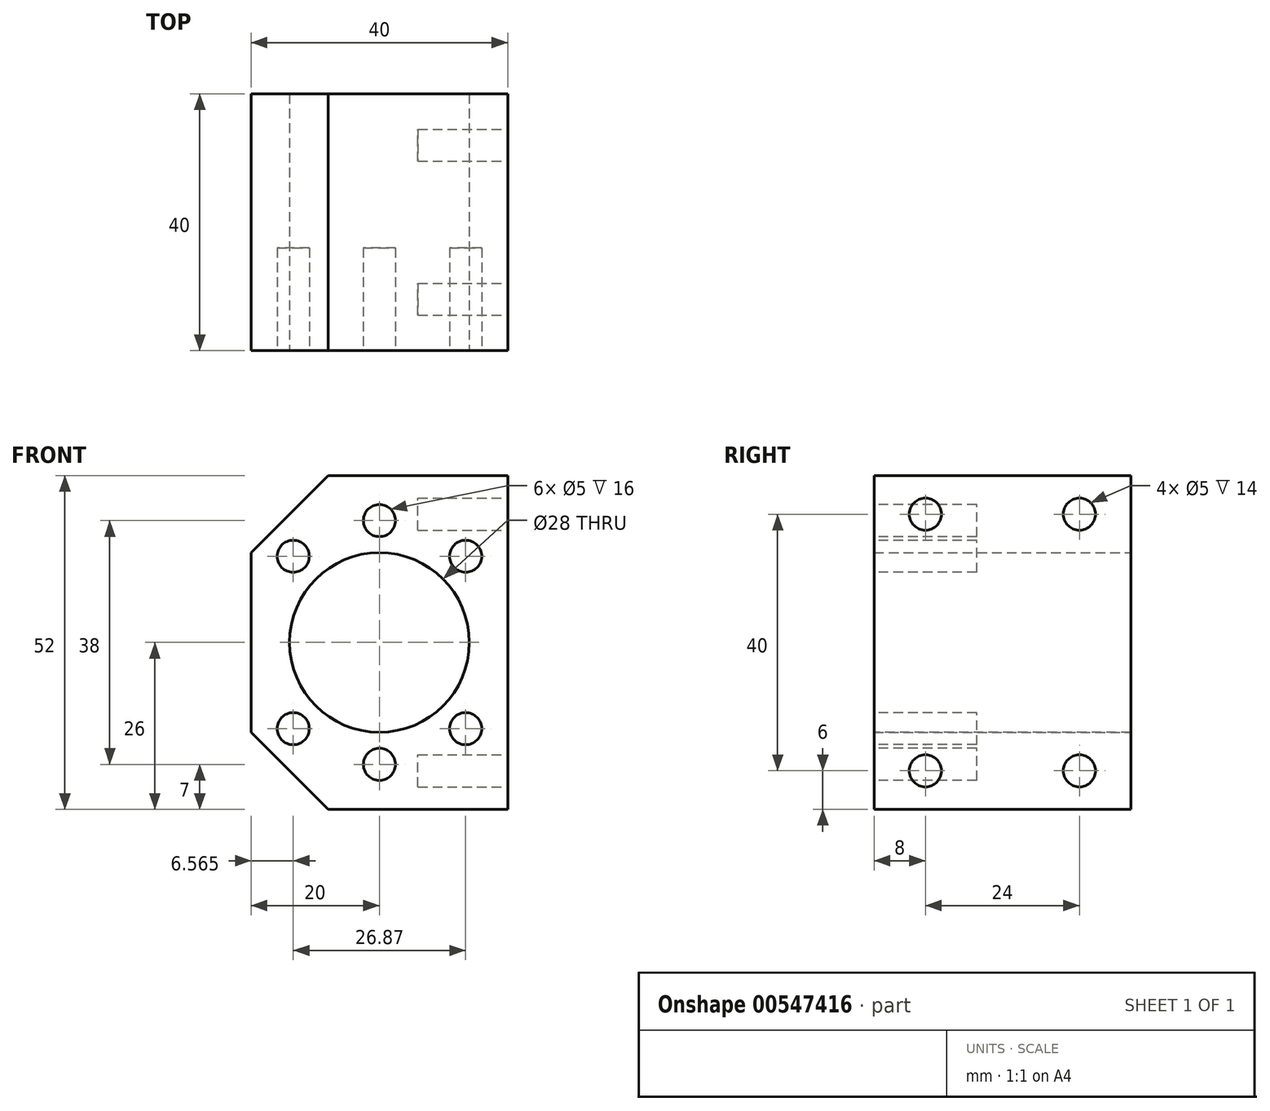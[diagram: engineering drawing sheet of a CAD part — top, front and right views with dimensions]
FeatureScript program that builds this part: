
annotation { "Feature Type Name" : "Feature", "Feature Type Description" : "" }
export const myFeature = defineFeature(function(context is Context, id is Id, definition is map)
    precondition{}
    {
        {
            var Q0;
            Q0=qCreatedBy(makeId("Front.planeOp"),FACE);
            var sketch = newSketch(context, id + "F0", { "sketchPlane" : qUnion([Q0])});
            skLineSegment(sketch, "E0.bottom", {"start": v(20, 26) * mm, "end": v(-8, 26) * mm});
            skLineSegment(sketch, "E0.top", {"start": v(20, -26) * mm, "end": v(-8, -26) * mm});
            skLineSegment(sketch, "E0.left", {"start": v(20, 26) * mm, "end": v(20, -26) * mm});
            skLineSegment(sketch, "E0.right", {"start": v(-20, 14) * mm, "end": v(-20, -14) * mm});
            skPoint(sketch, "E0.middle", {"position": v(0, 0) * mm});
            skLineSegment(sketch, "E1", {"start": v(-20, -14) * mm, "end": v(-8, -26) * mm});
            skLineSegment(sketch, "E2", {"start": v(-20, 14) * mm, "end": v(-8, 26) * mm});
            skPoint(sketch, "E3.orphan", {"position": v(-20, 26) * mm});
            skPoint(sketch, "E4.orphan", {"position": v(-20, -26) * mm});
            skSolve(sketch);
        }
        {
            var Q0;
            Q0 = qSketchRegion(id + "F0", true);
            extrude(context, id + "F1", {"entities" : qUnion([Q0]), "endBound" : BoundingType.SYMMETRIC, "depth" : 40 * mm, "offsetDistance" : 25 * mm});
        }
        {
            var Q0;
            Q0=makeQuery(id+"F1.opExtrude","CAP_FACE",FACE,{"disambiguationData":[OSD([sQuery(id+"F0.wireOp",EDGE,"E0.bottom"),sQuery(id+"F0.wireOp",EDGE,"E0.top"),sQuery(id+"F0.wireOp",EDGE,"E0.left"),sQuery(id+"F0.wireOp",EDGE,"E0.right"),sQuery(id+"F0.wireOp",EDGE,"E1"),sQuery(id+"F0.wireOp",EDGE,"E2")])],"isStart":false});
            var sketch = newSketch(context, id + "F2", { "sketchPlane" : qUnion([Q0])});
            skCircle(sketch, "E5", {"center": v(0, 0) * mm, "radius": 14 * mm});
            skSolve(sketch);
        }
        {
            var Q0;
            Q0 = qSketchRegion(id + "F2", true);
            extrude(context, id + "F3", {"entities" : qUnion([Q0]), "operationType" : NewBodyOperationType.REMOVE, "oppositeDirection" : true, "depth" : 40 * mm, "offsetDistance" : 25 * mm});
        }
        {
            var Q0;
            Q0=makeQuery(id+"F1.opExtrude","CAP_FACE",FACE,{"disambiguationData":[OSD([sQuery(id+"F0.wireOp",EDGE,"E0.bottom"),sQuery(id+"F0.wireOp",EDGE,"E0.top"),sQuery(id+"F0.wireOp",EDGE,"E0.left"),sQuery(id+"F0.wireOp",EDGE,"E0.right"),sQuery(id+"F0.wireOp",EDGE,"E1"),sQuery(id+"F0.wireOp",EDGE,"E2")])],"isStart":false});
            var sketch = newSketch(context, id + "F4", { "sketchPlane" : qUnion([Q0])});
            skCircle(sketch, "E6", {"center": v(-13.44, 13.44) * mm, "radius": 2.5 * mm});
            skCircle(sketch, "E7", {"center": v(13.44, 13.44) * mm, "radius": 2.5 * mm});
            skCircle(sketch, "E8", {"center": v(-13.44, -13.44) * mm, "radius": 2.5 * mm});
            skCircle(sketch, "E9", {"center": v(13.44, -13.44) * mm, "radius": 2.5 * mm});
            skCircle(sketch, "E10", {"center": v(0, 19) * mm, "radius": 2.5 * mm});
            skCircle(sketch, "E11", {"center": v(0, -19) * mm, "radius": 2.5 * mm});
            skSolve(sketch);
        }
        {
            var Q0;
            Q0 = qSketchRegion(id + "F4", true);
            extrude(context, id + "F5", {"entities" : qUnion([Q0]), "operationType" : NewBodyOperationType.REMOVE, "oppositeDirection" : true, "depth" : 16 * mm, "offsetDistance" : 25 * mm});
        }
        {
            var Q0;
            Q0=makeQuery(id+"F1.opExtrude","SWEPT_FACE",FACE,{"disambiguationData":[OSD([sQuery(id+"F0.wireOp",EDGE,"E0.left")])]});
            var sketch = newSketch(context, id + "F6", { "sketchPlane" : qUnion([Q0])});
            skCircle(sketch, "E12", {"center": v(-12, 20) * mm, "radius": 2.5 * mm});
            skCircle(sketch, "E13", {"center": v(12, 20) * mm, "radius": 2.5 * mm});
            skCircle(sketch, "E14", {"center": v(12, -20) * mm, "radius": 2.5 * mm});
            skCircle(sketch, "E15", {"center": v(-12, -20) * mm, "radius": 2.5 * mm});
            skSolve(sketch);
        }
        {
            var Q0;
            Q0 = qSketchRegion(id + "F6", true);
            extrude(context, id + "F7", {"entities" : qUnion([Q0]), "operationType" : NewBodyOperationType.REMOVE, "oppositeDirection" : true, "depth" : 14 * mm, "offsetDistance" : 25 * mm});
        }
    });
